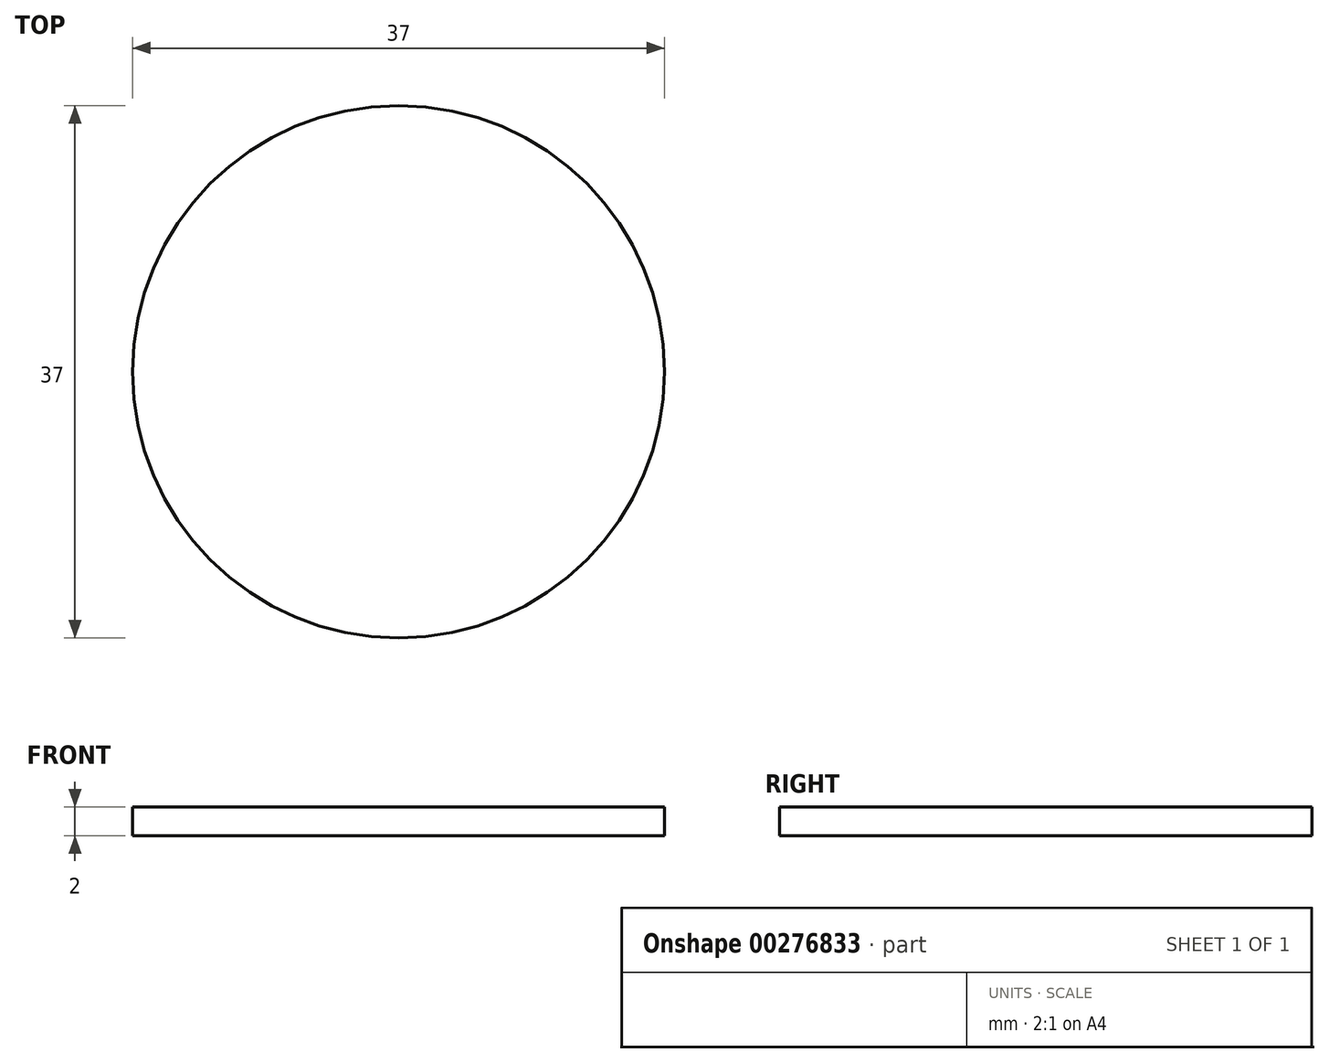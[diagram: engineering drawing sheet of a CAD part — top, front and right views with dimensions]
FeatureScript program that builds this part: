
annotation { "Feature Type Name" : "Feature", "Feature Type Description" : "" }
export const myFeature = defineFeature(function(context is Context, id is Id, definition is map)
    precondition{}
    {
        {
            var Q0;
            Q0=qCreatedBy(makeId("Top.planeOp"),FACE);
            var sketch = newSketch(context, id + "F0", { "sketchPlane" : qUnion([Q0])});
            skCircle(sketch, "E0", {"center": v(0, 0) * mm, "radius": 18.5 * mm});
            skSolve(sketch);
        }
        {
            var Q0;
            Q0 = qSketchRegion(id + "F0", true);
            extrude(context, id + "F1", {"entities" : qUnion([Q0]), "endBound" : BoundingType.SYMMETRIC, "depth" : 2 * mm});
        }
    });
